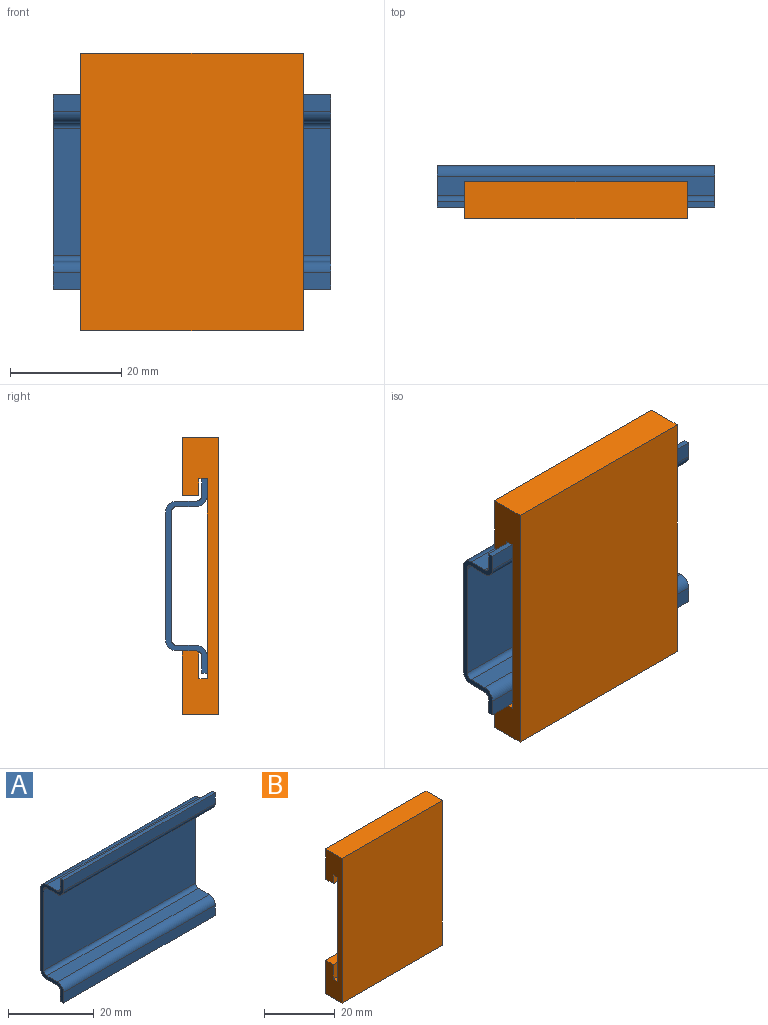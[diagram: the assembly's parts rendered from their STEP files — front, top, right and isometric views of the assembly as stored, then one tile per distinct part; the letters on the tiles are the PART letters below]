
ASSEMBLY  parts=2 mates=2
PART A: 22 faces, bbox 50x7.5x35 mm
  f0: plane 50x1mm, normal (0,0,1), area 50mm2, adj f1,f11,f12,f13
  f1: plane 50x3mm, normal (0,-1,0), area 150mm2, adj f0,f12,f13,f18
  f2: plane 50x3.5mm, normal (0,0,-1), area 175mm2, adj f12,f13,f14,f18
  f3: plane 50x23mm, normal (0,-1,0), area 1150mm2, adj f12,f13,f14,f15
  f4: plane 50x3.5mm, normal (0,0,1), area 175mm2, adj f12,f13,f15,f19
  f5: plane 50x3mm, normal (0,-1,0), area 150mm2, adj f6,f12,f13,f19
  f6: plane 50x1mm, normal (0,0,-1), area 50mm2, adj f5,f7,f12,f13
  f7: plane 50x3mm, normal (0,1,0), area 150mm2, adj f6,f12,f13,f16
  f8: plane 50x3.5mm, normal (0,0,-1), area 175mm2, adj f12,f13,f16,f20
  f9: plane 50x23mm, normal (0,1,0), area 1150mm2, adj f12,f13,f20,f21
  f10: plane 50x3.5mm, normal (0,0,1), area 175mm2, adj f12,f13,f17,f21
  f11: plane 50x3mm, normal (0,1,0), area 150mm2, adj f0,f12,f13,f17
  f12: plane 35x7.5mm, normal (1,0,0), area 45.4mm2, adj f0,f1,f2,f3,f4,f5,f6,f7
  f13: plane 35x7.5mm, normal (-1,0,0), area 45.4mm2, adj f0,f1,f2,f3,f4,f5,f6,f7
  f14: cylinder r=1mm len=50mm, axis (1,0,0), area 78.5mm2, adj f2,f3,f12,f13
  f15: cylinder r=1mm len=50mm, axis (1,0,0), area 78.5mm2, adj f3,f4,f12,f13
  f16: cylinder r=1mm len=50mm, axis (1,0,0), area 78.5mm2, adj f7,f8,f12,f13
  f17: cylinder r=1mm len=50mm, axis (1,0,0), area 78.5mm2, adj f10,f11,f12,f13
  f18: cylinder r=2mm len=50mm, axis (-1,0,0), area 157.1mm2, adj f1,f2,f12,f13
  f19: cylinder r=2mm len=50mm, axis (-1,0,0), area 157.1mm2, adj f4,f5,f12,f13
  f20: cylinder r=2mm len=50mm, axis (-1,0,0), area 157.1mm2, adj f8,f9,f12,f13
  f21: cylinder r=2mm len=50mm, axis (-1,0,0), area 157.1mm2, adj f9,f10,f12,f13
PART B: 14 faces, bbox 40x6.5x50 mm
  f0: plane 40x3mm, normal (0,0,-1), area 120mm2, adj f1,f11,f12,f13
  f1: plane 40x10.5mm, normal (0,1,0), area 420mm2, adj f0,f2,f12,f13
  f2: plane 40x6.5mm, normal (0,0,1), area 260mm2, adj f1,f3,f12,f13
  f3: plane 50x40mm, normal (0,-1,0), area 2000mm2, adj f2,f4,f12,f13
  f4: plane 40x6.5mm, normal (0,0,-1), area 260mm2, adj f3,f5,f12,f13
  f5: plane 40x11.5mm, normal (0,1,0), area 460mm2, adj f4,f6,f12,f13
  f6: plane 40x3mm, normal (0,0,1), area 120mm2, adj f5,f7,f12,f13
  f7: plane 40x5mm, normal (0,-1,0), area 200mm2, adj f6,f8,f12,f13
  f8: plane 40x1.5mm, normal (0,0,1), area 60mm2, adj f7,f9,f12,f13
  f9: plane 40x36mm, normal (0,1,0), area 1440mm2, adj f8,f10,f12,f13
  f10: plane 40x1.5mm, normal (0,0,-1), area 60mm2, adj f9,f11,f12,f13
  f11: plane 40x3mm, normal (0,-1,0), area 120mm2, adj f0,f10,f12,f13
  f12: plane 50x6.5mm, normal (1,0,0), area 187mm2, adj f0,f1,f2,f3,f4,f5,f6,f7
  f13: plane 50x6.5mm, normal (-1,0,0), area 187mm2, adj f0,f1,f2,f3,f4,f5,f6,f7
PLACE A t=(-0.12,-0.42,0.99)mm fixed
PLACE B t=(-0.12,-2.42,0.99)mm
MATE planar B.f9 <-> A.f1  axis (0,1,0) through (-0.12,-6.92,0.49)mm
MATE planar A.f0 <-> B.f10  axis (0,0,1) through (-0.12,-6.42,18.49)mm
